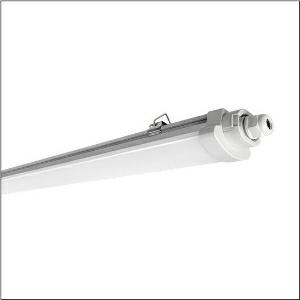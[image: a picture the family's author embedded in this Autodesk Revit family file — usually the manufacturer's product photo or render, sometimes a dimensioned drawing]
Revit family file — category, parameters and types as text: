
# Revit family: monsun_41_51fk20mn460a
name_source: partatom
category: Lighting Fixtures
units: mm (PartAtom-declared; Revit-internal decimal feet)

## family parameters
Cut with Voids When Loaded = No
Host = Face
Light Source = No
Part Type = Normal
Room Calculation Point = No
Round Connector Dimension = Use Diameter
Shared = No

## types (1)
- --- (1 x LED, 6000 lm, 46 W, 4000K)
    Apparent Load = 46 VA
    CIE Flux Codes = 44 74 91 91 100
    Color Rendering = 80
    Color Temperature = 4000K
    Default Elevation = 1800 mm
    Description = Monsun 41, damp-proof luminaire, primary optical cover: diffuser, of PC, frosted, light emission: direct distribution, primary light characteristic: symmetric, installation type: suspended mounting, surface-mounted, LED, rated luminous flux: 6.000lm, luminous efficacy: 130lm/W, light colour: 840, colour temperature: 4000K, control gear: ON/OFF Multilumen, with terminal, 3-pole, mains connection: 220..240V, AC, 50/60Hz, rated input power: 46W, housing, luminaire housing, of PC, grey, length: 1.500mm, width: 79mm, height: 52mm, end cap, of PC, grey, ceiling mounting element, of stainless steel (V2A), protection rating (complete): IP65, insulation class (complete): insulation class II (safety insulation), certification: CE, UKCA, protection symbol: D, impact resistance: IK08, permissible operating ambient temperature: -20..+35°C, corresponds to IFS (International Featured Standards) requirements for safety and quality in the food industry, contact your sales advisor before using the luminaires in applications with unclear chemical exposure, large temperature fluctuations or condensation-forming humidity, packaging unit: 1 piece
    Height = 54 mm
    Lamp = 1 x LED
    Lamp Light Flux = 6000 lm
    Lamp Power = 46 W
    Lamp count = 1
    Length = 1500 mm
    Luminous efficacy = 130 lm/W
    Manufacturer = Siteco
    ModVariant = No
    Model = 51FK20MN460A
    Mounting Place = Ceiling
    Mounting Type = Surface mounted
    Number of Poles = 1
    OnlyDefault = Yes
    Power Factor = 1
    Product Name = Monsun 41
    Product group = damp-proof luminaire
    ProductGroupID = 300
    Protection Class = Protection class II
    Protection Degree = IP 65
    RLX_Detail_Level = 1
    RLX_Emergency_Light_Flux = 0 lm
    RLX_Emergency_Type = 0
    RLX_Emergency_Type_DB = No
    RlxData = <blob elided: 28913 chars, md5=ec61e856>
    Socket = socket
    Standby Power = 0 W
    System Light Flux = 6000 lm
    System Power = 46 W
    Type Comments = factory setting: luminous flux: 100 % | (HIGH)
    Type Image = l_1007037.jpg
    URL = http://relux.com
    VarID = @adj_174179
    Voltage = 0 V
    Weight = 0.00 kg
    Width = 79 mm

## geometry (parser evidence)
native form markers: Blend x4, Sweep x12
no freeform markers — native parametric forms only
